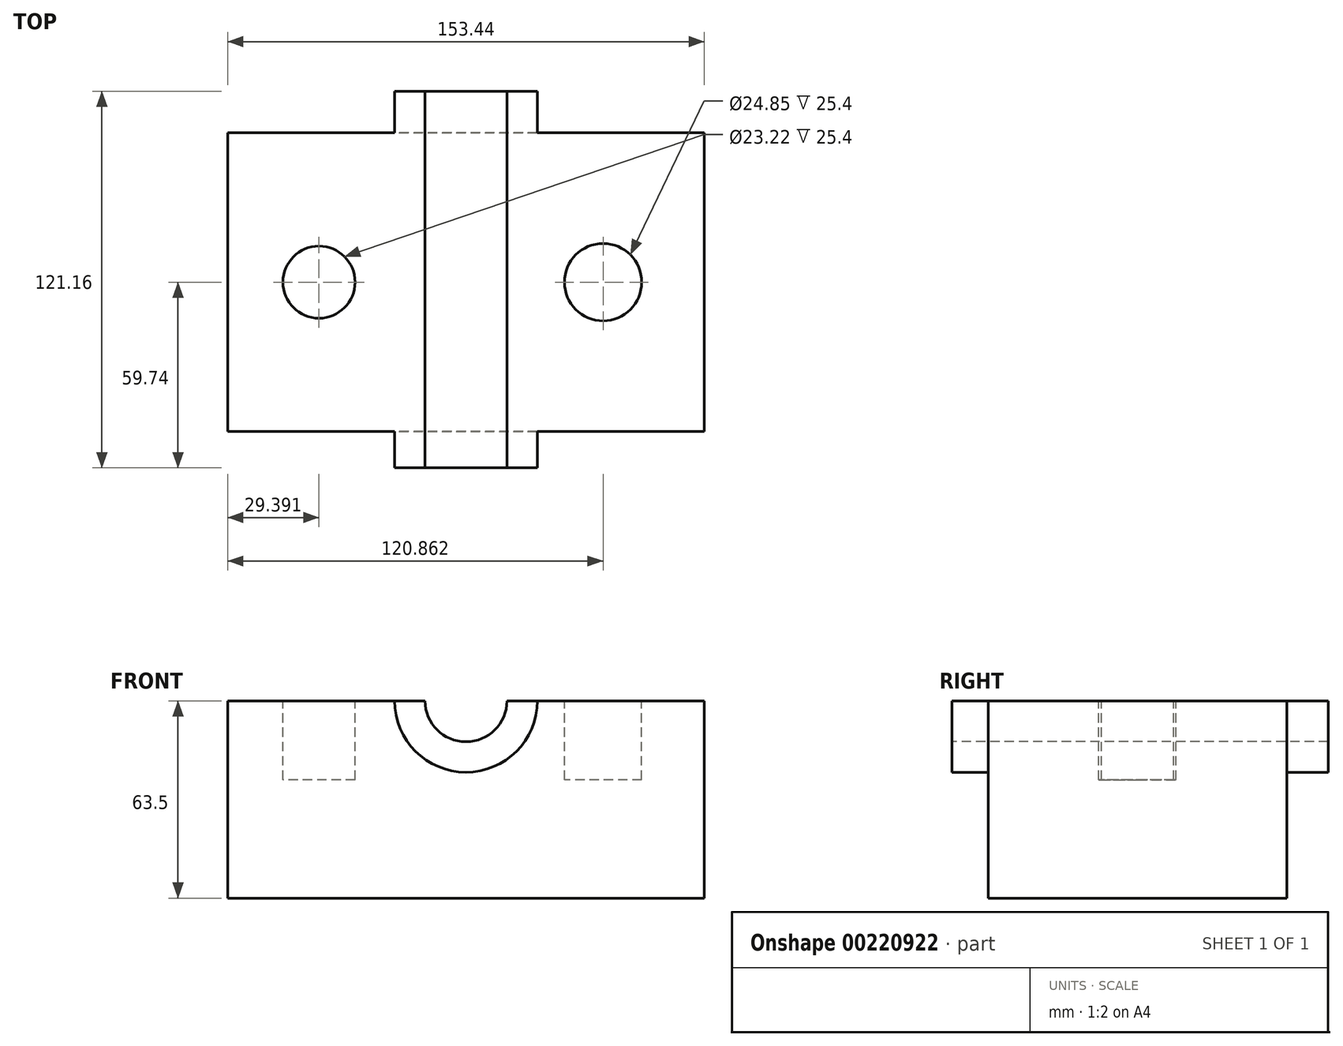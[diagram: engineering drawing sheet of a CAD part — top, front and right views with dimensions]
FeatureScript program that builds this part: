
annotation { "Feature Type Name" : "Feature", "Feature Type Description" : "" }
export const myFeature = defineFeature(function(context is Context, id is Id, definition is map)
    precondition{}
    {
        {
            var Q0;
            Q0=qCreatedBy(makeId("Top.planeOp"),FACE);
            var sketch = newSketch(context, id + "F0", { "sketchPlane" : qUnion([Q0])});
            skLineSegment(sketch, "E0.bottom", {"start": v(-76.72, 48.05) * mm, "end": v(76.72, 48.05) * mm});
            skLineSegment(sketch, "E0.top", {"start": v(-76.72, -48.05) * mm, "end": v(76.72, -48.05) * mm});
            skLineSegment(sketch, "E0.left", {"start": v(-76.72, 48.05) * mm, "end": v(-76.72, -48.05) * mm});
            skLineSegment(sketch, "E0.right", {"start": v(76.72, 48.05) * mm, "end": v(76.72, -48.05) * mm});
            skPoint(sketch, "E0.middle", {"position": v(0, 0) * mm});
            skSolve(sketch);
        }
        {
            var Q0;
            Q0=makeQuery(id+"F0.imprint","IMPRINT",FACE,{"disambiguationData":[TD([[makeQuery(id+"F0.imprint","IMPRINT",EDGE,{"derivedFrom":sQuery(id+"F0.wireOp",EDGE,"E0.bottom")}),-1.0]])]});
            extrude(context, id + "F1", {"entities" : qUnion([Q0]), "depth" : 63.5 * mm});
        }
        {
            var Q0;
            Q0=makeQuery(id+"F1.opExtrude","CAP_FACE",FACE,{"disambiguationData":[OSD([sQuery(id+"F0.wireOp",EDGE,"E0.bottom"),sQuery(id+"F0.wireOp",EDGE,"E0.top"),sQuery(id+"F0.wireOp",EDGE,"E0.left"),sQuery(id+"F0.wireOp",EDGE,"E0.right")])],"isStart":false});
            var sketch = newSketch(context, id + "F2", { "sketchPlane" : qUnion([Q0])});
            skCircle(sketch, "E1", {"center": v(44.14, 0) * mm, "radius": 12.43 * mm});
            skCircle(sketch, "E2", {"center": v(-47.33, 0) * mm, "radius": 11.6 * mm});
            skSolve(sketch);
        }
        {
            var Q0;
            Q0=makeQuery(id+"F2.imprint","IMPRINT",FACE,{"disambiguationData":[TD([[makeQuery(id+"F2.imprint","IMPRINT",EDGE,{"derivedFrom":sQuery(id+"F2.wireOp",EDGE,"E2")}),1.0]])]});
            var Q1;
            Q1=makeQuery(id+"F2.imprint","IMPRINT",FACE,{"disambiguationData":[TD([[makeQuery(id+"F2.imprint","IMPRINT",EDGE,{"derivedFrom":sQuery(id+"F2.wireOp",EDGE,"E1")}),1.0]])]});
            var Q2;
            Q2=makeQuery(id+"F1.opExtrude","CAP_FACE",FACE,{"disambiguationData":[OSD([sQuery(id+"F0.wireOp",EDGE,"E0.bottom"),sQuery(id+"F0.wireOp",EDGE,"E0.top"),sQuery(id+"F0.wireOp",EDGE,"E0.left"),sQuery(id+"F0.wireOp",EDGE,"E0.right")])],"isStart":false});
            extrude(context, id + "F3", {"entities" : qUnion([Q0, Q1]), "operationType" : NewBodyOperationType.REMOVE, "oppositeDirection" : true, "endBoundEntityFace" : qUnion([Q2]), "depth" : 25.4 * mm});
        }
        {
            var Q0;
            Q0=makeQuery(id+"F1.opExtrude","SWEPT_FACE",FACE,{"disambiguationData":[OSD([sQuery(id+"F0.wireOp",EDGE,"E0.top")])]});
            var sketch = newSketch(context, id + "F4", { "sketchPlane" : qUnion([Q0])});
            skCircle(sketch, "E3", {"center": v(0, 63.5) * mm, "radius": 22.98 * mm});
            skCircle(sketch, "E4", {"center": v(0, 63.5) * mm, "radius": 13.19 * mm});
            skSolve(sketch);
        }
        {
            var Q0;
            {var subQ0=sQuery(id+"F4.wireOp",EDGE,"E4");var subQ1=makeQuery(id+"F1.opExtrude","CAP_EDGE",EDGE,{"disambiguationData":[OSD([sQuery(id+"F0.wireOp",EDGE,"E0.top")])],"isStart":false});var subQ2=makeQuery(id+"F4.imprint","INTERSECT",VERTEX,{"disambiguationData":[OD(0.0)],"derivedFrom":[subQ1,subQ0]});Q0=makeQuery(id+"F4.imprint","IMPRINT",FACE,{"disambiguationData":[TD([[makeQuery(id+"F4.imprint","IMPRINT",EDGE,{"disambiguationData":[TD([[subQ2,-1.0]])],"derivedFrom":subQ0}),1.0]])]});}
            extrude(context, id + "F5", {"entities" : qUnion([Q0]), "operationType" : NewBodyOperationType.REMOVE, "endBound" : BoundingType.THROUGH_ALL, "oppositeDirection" : true, "depth" : 25.4 * mm});
        }
        {
            var Q0;
            {var subQ0=sQuery(id+"F4.wireOp",EDGE,"E3");var subQ1=makeQuery(id+"F1.opExtrude","CAP_EDGE",EDGE,{"disambiguationData":[OSD([sQuery(id+"F0.wireOp",EDGE,"E0.top")])],"isStart":false});var subQ2=makeQuery(id+"F4.imprint","INTERSECT",VERTEX,{"disambiguationData":[OD(0.0)],"derivedFrom":[subQ1,subQ0]});Q0=makeQuery(id+"F4.imprint","IMPRINT",FACE,{"disambiguationData":[TD([[makeQuery(id+"F4.imprint","IMPRINT",EDGE,{"disambiguationData":[TD([[subQ2,-1.0]])],"derivedFrom":subQ0}),1.0]])]});}
            extrude(context, id + "F6", {"entities" : qUnion([Q0]), "operationType" : NewBodyOperationType.ADD, "oppositeDirection" : true, "depth" : 109.47 * mm, "hasSecondDirection" : true, "secondDirectionOppositeDirection" : false, "secondDirectionDepth" : 11.68 * mm});
        }
    });
